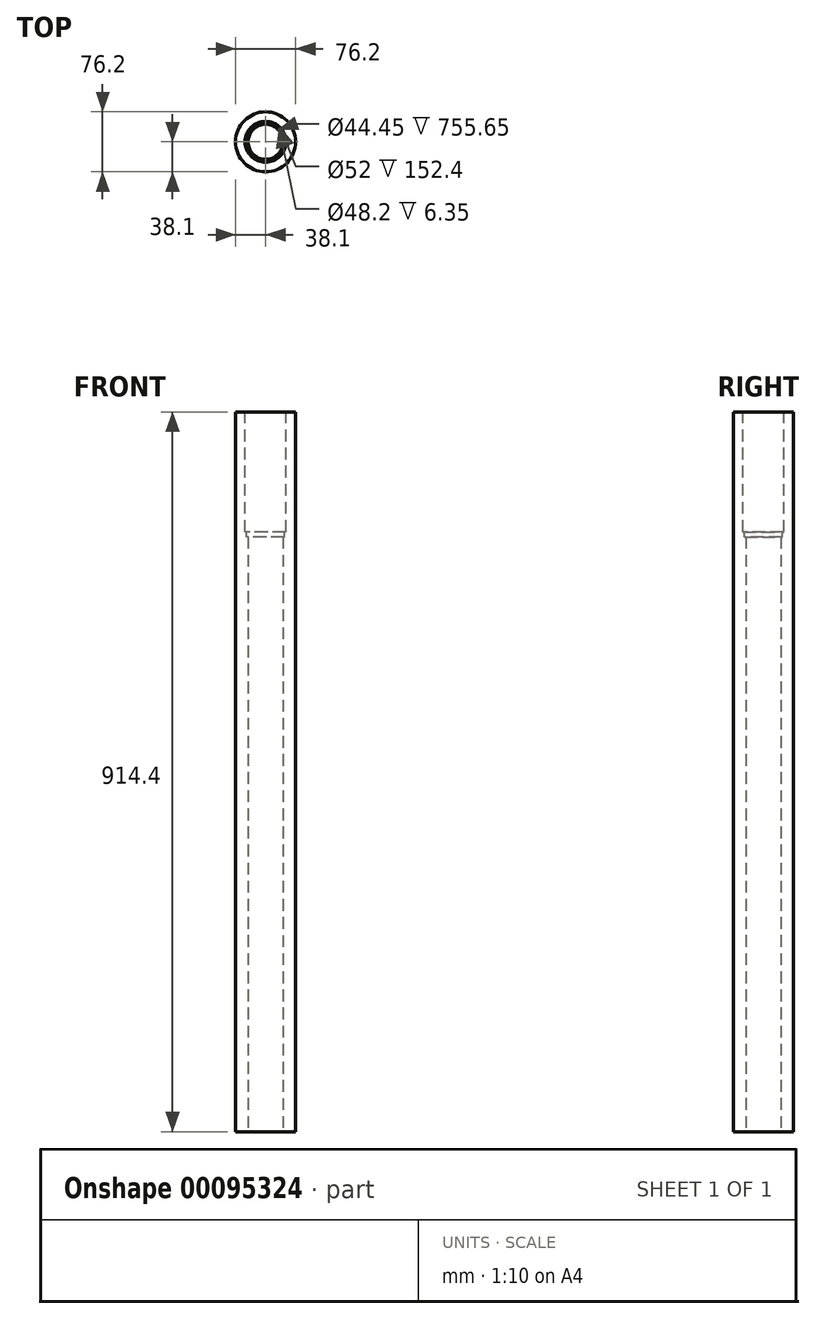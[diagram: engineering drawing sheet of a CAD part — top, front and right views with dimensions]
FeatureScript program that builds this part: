
annotation { "Feature Type Name" : "Feature", "Feature Type Description" : "" }
export const myFeature = defineFeature(function(context is Context, id is Id, definition is map)
    precondition{}
    {
        {
            var Q0;
            Q0=qCreatedBy(makeId("Top.planeOp"),FACE);
            var sketch = newSketch(context, id + "F0", { "sketchPlane" : qUnion([Q0])});
            skCircle(sketch, "E0", {"center": v(0, 0) * mm, "radius": 38.1 * mm});
            skCircle(sketch, "E1", {"center": v(0, 0) * mm, "radius": 22.23 * mm});
            skSolve(sketch);
        }
        {
            var Q0;
            Q0=makeQuery(id+"F0.imprint","IMPRINT",FACE,{"disambiguationData":[TD([[makeQuery(id+"F0.imprint","IMPRINT",EDGE,{"derivedFrom":sQuery(id+"F0.wireOp",EDGE,"E0")}),1.0]])]});
            extrude(context, id + "F1", {"entities" : qUnion([Q0]), "depth" : 914.4 * mm});
        }
        {
            var Q0;
            Q0=makeQuery(id+"F1.opExtrude","CAP_FACE",FACE,{"disambiguationData":[OSD([sQuery(id+"F0.wireOp",EDGE,"E0")])],"isStart":false});
            var sketch = newSketch(context, id + "F2", { "sketchPlane" : qUnion([Q0])});
            skCircle(sketch, "E2", {"center": v(0, 0) * mm, "radius": 20.32 * mm});
            skCircle(sketch, "E3.0", {"center": v(0, 0) * mm, "radius": 38.1 * mm});
            skSolve(sketch);
        }
        {
            var Q0;
            Q0=makeQuery(id+"F2.imprint","IMPRINT",FACE,{"disambiguationData":[TD([[makeQuery(id+"F2.imprint","IMPRINT",EDGE,{"derivedFrom":sQuery(id+"F2.wireOp",EDGE,"E3.0")}),1.0]])]});
            var sketch = newSketch(context, id + "F3", { "sketchPlane" : qUnion([Q0])});
            skCircle(sketch, "E4", {"center": v(0, 0) * mm, "radius": 26 * mm});
            skSolve(sketch);
        }
        {
            var Q0;
            Q0=makeQuery(id+"F3.imprint","IMPRINT",FACE,{"disambiguationData":[TD([[makeQuery(id+"F3.imprint","IMPRINT",EDGE,{"derivedFrom":sQuery(id+"F3.wireOp",EDGE,"E4")}),1.0]])]});
            var Q1;
            Q1=makeQuery(id+"F3.imprint","IMPRINT",FACE,{"disambiguationData":[TD([[makeQuery(id+"F3.imprint","IMPRINT",EDGE,{"derivedFrom":sQuery(id+"F3.wireOp",EDGE,"Epeh9n8A-D37p-aXoc-y6pM-pkkXXkpryhlQ")}),1.0]])]});
            extrude(context, id + "F4", {"entities" : qUnion([Q0, Q1]), "operationType" : NewBodyOperationType.REMOVE, "oppositeDirection" : true, "depth" : 152.4 * mm});
        }
        {
            var Q0;
            Q0=makeQuery(id+"F4.boolean.opBoolean","COPY",FACE,{"derivedFrom":makeQuery(id+"F4.opExtrude","CAP_FACE",FACE,{"disambiguationData":[OSD([sQuery(id+"F0.wireOp",EDGE,"E1"),sQuery(id+"F3.wireOp",EDGE,"E4")])],"isStart":false})});
            var sketch = newSketch(context, id + "F5", { "sketchPlane" : qUnion([Q0])});
            skCircle(sketch, "E5", {"center": v(0, 0) * mm, "radius": 24.1 * mm});
            skSolve(sketch);
        }
        {
            var Q0;
            Q0 = qSketchRegion(id + "F5", true);
            extrude(context, id + "F6", {"entities" : qUnion([Q0]), "operationType" : NewBodyOperationType.REMOVE, "oppositeDirection" : true, "depth" : 6.35 * mm});
        }
    });
